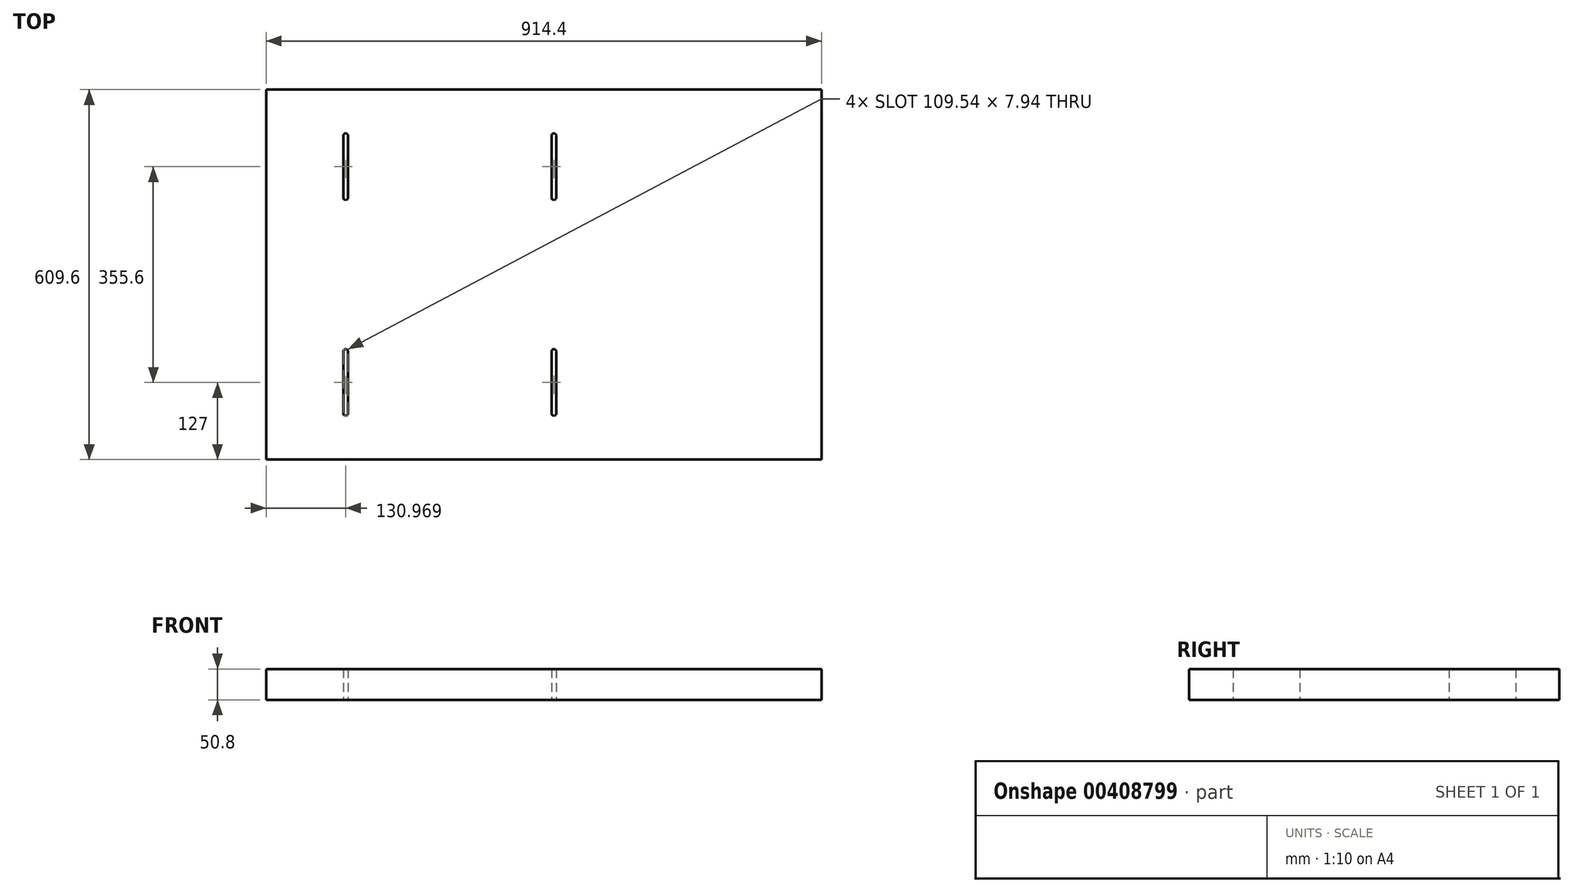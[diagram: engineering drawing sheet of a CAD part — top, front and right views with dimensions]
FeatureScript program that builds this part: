
annotation { "Feature Type Name" : "Feature", "Feature Type Description" : "" }
export const myFeature = defineFeature(function(context is Context, id is Id, definition is map)
    precondition{}
    {
        {
            var Q0;
            Q0=qCreatedBy(makeId("Top.planeOp"),FACE);
            var sketch = newSketch(context, id + "F0", { "sketchPlane" : qUnion([Q0])});
            skLineSegment(sketch, "E0.bottom", {"start": v(457.2, 304.8) * mm, "end": v(-457.2, 304.8) * mm});
            skLineSegment(sketch, "E0.top", {"start": v(457.2, -304.8) * mm, "end": v(-457.2, -304.8) * mm});
            skLineSegment(sketch, "E0.left", {"start": v(457.2, 304.8) * mm, "end": v(457.2, -304.8) * mm});
            skLineSegment(sketch, "E0.right", {"start": v(-457.2, 304.8) * mm, "end": v(-457.2, -304.8) * mm});
            skPoint(sketch, "E0.middle", {"position": v(0, 0) * mm});
            skSolve(sketch);
        }
        {
            var Q0;
            Q0 = qSketchRegion(id + "F0", true);
            extrude(context, id + "F1", {"entities" : qUnion([Q0]), "depth" : 50.8 * mm});
        }
        {
            var Q0;
            Q0=qCreatedBy(makeId("Top.planeOp"),FACE);
            var sketch = newSketch(context, id + "F2", { "sketchPlane" : qUnion([Q0])});
            skLineSegment(sketch, "E1.left", {"start": v(-322.26, 228.6) * mm, "end": v(-322.26, 127) * mm});
            skLineSegment(sketch, "E1.right", {"start": v(-330.2, 228.6) * mm, "end": v(-330.2, 127) * mm});
            skPoint(sketch, "E1.middle", {"position": v(-326.23, 177.8) * mm});
            skArc(sketch, "E2", {"start": v(-330.2, 228.6) * mm, "mid": v(-326.23, 232.57) * mm, "end": v(-322.26, 228.6) * mm});
            skArc(sketch, "E3", {"start": v(-322.26, 127) * mm, "mid": v(-326.23, 123.03) * mm, "end": v(-330.2, 127) * mm});
            skLineSegment(sketch, "E4.left", {"start": v(20.64, 228.6) * mm, "end": v(20.64, 127) * mm});
            skLineSegment(sketch, "E4.right", {"start": v(12.7, 228.6) * mm, "end": v(12.7, 127) * mm});
            skPoint(sketch, "E4.middle", {"position": v(16.67, 177.8) * mm});
            skArc(sketch, "E5", {"start": v(12.7, 228.6) * mm, "mid": v(16.67, 232.57) * mm, "end": v(20.64, 228.6) * mm});
            skArc(sketch, "E6", {"start": v(20.64, 127) * mm, "mid": v(16.67, 123.03) * mm, "end": v(12.7, 127) * mm});
            skLineSegment(sketch, "E7.left", {"start": v(-322.26, -127) * mm, "end": v(-322.26, -228.6) * mm});
            skLineSegment(sketch, "E7.right", {"start": v(-330.2, -127) * mm, "end": v(-330.2, -228.6) * mm});
            skPoint(sketch, "E7.middle", {"position": v(-326.23, -177.8) * mm});
            skArc(sketch, "E8", {"start": v(-330.2, -127) * mm, "mid": v(-326.23, -123.03) * mm, "end": v(-322.26, -127) * mm});
            skArc(sketch, "E9", {"start": v(-322.26, -228.6) * mm, "mid": v(-326.23, -232.57) * mm, "end": v(-330.2, -228.6) * mm});
            skLineSegment(sketch, "E10.left", {"start": v(20.64, -127) * mm, "end": v(20.64, -228.6) * mm});
            skLineSegment(sketch, "E10.right", {"start": v(12.7, -127) * mm, "end": v(12.7, -228.6) * mm});
            skPoint(sketch, "E10.middle", {"position": v(16.67, -177.8) * mm});
            skArc(sketch, "E11", {"start": v(12.7, -127) * mm, "mid": v(16.67, -123.03) * mm, "end": v(20.64, -127) * mm});
            skArc(sketch, "E12", {"start": v(20.64, -228.6) * mm, "mid": v(16.67, -232.57) * mm, "end": v(12.7, -228.6) * mm});
            skSolve(sketch);
        }
        {
            var Q0;
            Q0 = qSketchRegion(id + "F2", true);
            extrude(context, id + "F3", {"entities" : qUnion([Q0]), "operationType" : NewBodyOperationType.REMOVE, "depth" : 50.8 * mm});
        }
    });
